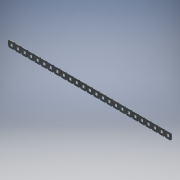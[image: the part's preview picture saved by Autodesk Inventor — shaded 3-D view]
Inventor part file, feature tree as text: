
AUTODESK INVENTOR PART (.ipt)
format: ipt  version: 2018 (Build 220112000, 112)  size: 471,552 bytes
history: native  units: mm (DEFAULTED — no unit token found)
features: other x26, extrude x25, pattern_linear x2, sketch x2, sheet_metal_op x1
ambient origin geometry x8: Origin, YZ Plane, XZ Plane, XY Plane, X Axis, Y Axis, Z Axis, Center Point
bodies: Solid1 (feature_tree)
feature tree (56):
  sheet_metal_op  "Face1"
  pattern_linear  "Rectangular Pattern1"  Spacing1=1.905mm  [1 undecoded]
  pattern_linear  "Rectangular Pattern2"  Spacing1=1.905mm  [1 undecoded]
  sketch  "Sketch1"  dims[d0=12.7mm]
  other  "Plate1"
  sketch  "Sketch4"  dims[d1=12.7mm d2=1.905mm d3=1.905mm d4=1.905mm d5=1.905mm d6=1.905mm d7=1.905mm d8=1.905mm d9=1.905mm d10=4.6228mm d11=4.6228mm d12=4.064mm d13=4.064mm d14=1.27mm d15=250.0mm d17=12.7mm d18=0.508mm d19=25.4mm d20=0.0mm d21=250.0mm d23=12.7mm d24=0.0mm d25=0.0mm d26=0.0mm d27=0.0mm d28=0.0mm d29=0.0mm d30=0.0mm d31=0.0mm d32=0.0mm d33=0.0mm d34=0.0mm d35=0.0mm d36=0.0mm d37=0.0mm d38=0.0mm d39=0.0mm d40=0.0mm d41=0.0mm d42=0.0mm d43=0.0mm d44=0.0mm d45=0.0mm d46=0.0mm d47=0.0mm d48=0.0mm d49=0.0mm d50=0.0mm d51=0.0mm d52=0.0mm d53=0.0mm d54=0.0mm d55=0.0mm d56=0.0mm d57=0.0mm d58=0.0mm d59=0.0mm d60=0.0mm d61=0.0mm d62=0.0mm d63=0.0mm d64=1.27mm]
  other  "Srf1"
  other  "Srf2"
  other  "Srf3"
  other  "Srf4"
  other  "Srf5"
  other  "Srf6"
  other  "Srf7"
  other  "Srf8"
  other  "Srf9"
  other  "Srf10"
  other  "Srf11"
  other  "Srf12"
  other  "Srf13"
  other  "Srf14"
  other  "Srf15"
  other  "Srf16"
  other  "Srf17"
  other  "Srf18"
  other  "Srf19"
  other  "Srf20"
  other  "Srf21"
  other  "Srf22"
  other  "Srf23"
  other  "Srf24"
  other  "Srf25"
  extrude  "ExtrusionSrf1"  Depth=1.27mm
  extrude  "ExtrusionSrf2"  Depth=1.27mm
  extrude  "ExtrusionSrf3"  Depth=1.27mm
  extrude  "ExtrusionSrf4"  Depth=1.27mm
  extrude  "ExtrusionSrf5"  Depth=1.27mm
  extrude  "ExtrusionSrf6"  Depth=1.27mm
  extrude  "ExtrusionSrf7"  Depth=4.6228mm
  extrude  "ExtrusionSrf8"  Depth=4.6228mm
  extrude  "ExtrusionSrf9"  Depth=4.064mm
  extrude  "ExtrusionSrf10"  Depth=4.064mm
  extrude  "ExtrusionSrf11"  Depth=1.27mm
  extrude  "ExtrusionSrf12"  Depth=250.0mm
  extrude  "ExtrusionSrf13"  Depth=0.508mm
  extrude  "ExtrusionSrf14"  Depth=25.4mm TaperAngle=0.0deg
  extrude  "ExtrusionSrf15"  Depth=250.0mm
  extrude  "ExtrusionSrf16"  Depth=1.27mm
  extrude  "ExtrusionSrf17"  [1 undecoded]
  extrude  "ExtrusionSrf18"  [1 undecoded]
  extrude  "ExtrusionSrf19"  [1 undecoded]
  extrude  "ExtrusionSrf20"  [1 undecoded]
  extrude  "ExtrusionSrf21"  [1 undecoded]
  extrude  "ExtrusionSrf22"  [1 undecoded]
  extrude  "ExtrusionSrf23"  [1 undecoded]
  extrude  "ExtrusionSrf24"  [1 undecoded]
  extrude  "ExtrusionSrf25"  [1 undecoded]
note: 11 required parameter values undecoded (feature->parameter linkage not recoverable at this tier; creation-order binding heuristic only, values carry confidence <= 0.55)
